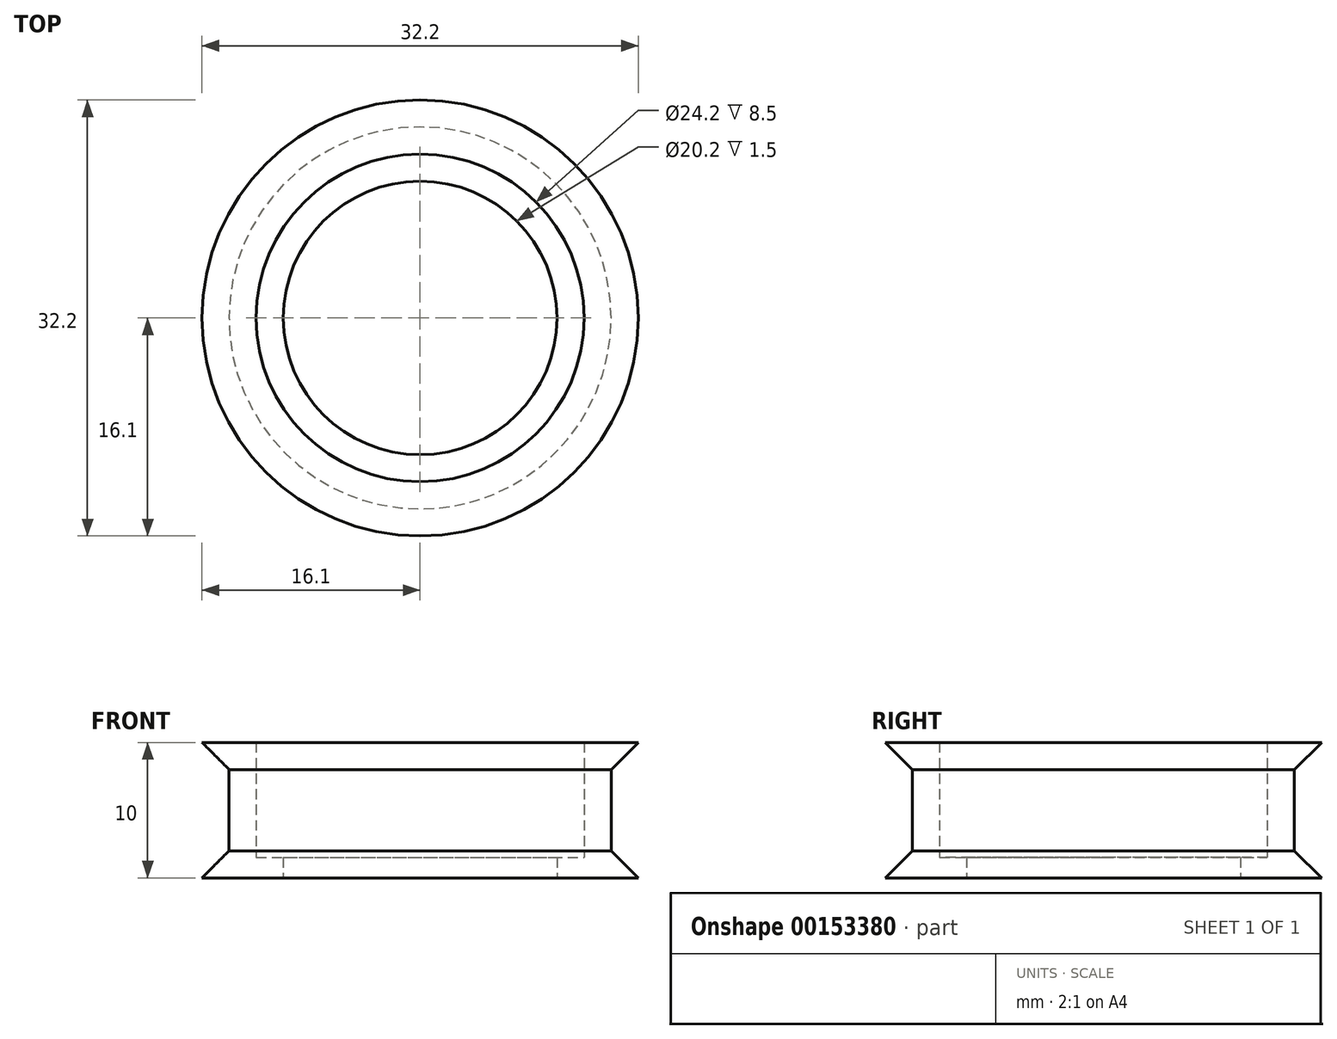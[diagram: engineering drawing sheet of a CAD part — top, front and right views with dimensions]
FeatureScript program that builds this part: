
annotation { "Feature Type Name" : "Feature", "Feature Type Description" : "" }
export const myFeature = defineFeature(function(context is Context, id is Id, definition is map)
    precondition{}
    {
        {
            var Q0;
            Q0=qCreatedBy(makeId("Front.planeOp"),FACE);
            var sketch = newSketch(context, id + "F0", { "sketchPlane" : qUnion([Q0])});
            skLineSegment(sketch, "E0", {"start": v(12.1, 4.8) * mm, "end": v(16.1, 4.8) * mm});
            skLineSegment(sketch, "E1", {"start": v(16.1, 4.8) * mm, "end": v(14.1, 2.8) * mm});
            skLineSegment(sketch, "E2", {"start": v(14.1, 2.8) * mm, "end": v(14.1, -3.2) * mm});
            skLineSegment(sketch, "E3", {"start": v(14.1, -3.2) * mm, "end": v(16.1, -5.2) * mm});
            skLineSegment(sketch, "E4", {"start": v(16.1, -5.2) * mm, "end": v(12.1, -5.2) * mm});
            skLineSegment(sketch, "E5", {"start": v(12.1, -5.2) * mm, "end": v(12.1, 4.8) * mm});
            skLineSegment(sketch, "E6", {"start": v(0, -3.77) * mm, "end": v(0, 4.95) * mm, "construction": true});
            skLineSegment(sketch, "E7.bottom", {"start": v(12.1, -5.2) * mm, "end": v(10.1, -5.2) * mm});
            skLineSegment(sketch, "E7.top", {"start": v(12.1, -3.7) * mm, "end": v(10.1, -3.7) * mm});
            skLineSegment(sketch, "E7.left", {"start": v(12.1, -5.2) * mm, "end": v(12.1, -3.7) * mm});
            skLineSegment(sketch, "E7.right", {"start": v(10.1, -5.2) * mm, "end": v(10.1, -3.7) * mm});
            skSolve(sketch);
        }
        {
            var Q0;
            Q0=qSketchRegion(id+"F0",true);
            var Q1;
            Q1=sQuery(id+"F0.wireOp",EDGE,"E6");
            revolve(context, id + "F1", {"entities" : qUnion([Q0]), "axis" : qUnion([Q1]), "revolveType" : RevolveType.FULL});
        }
    });
